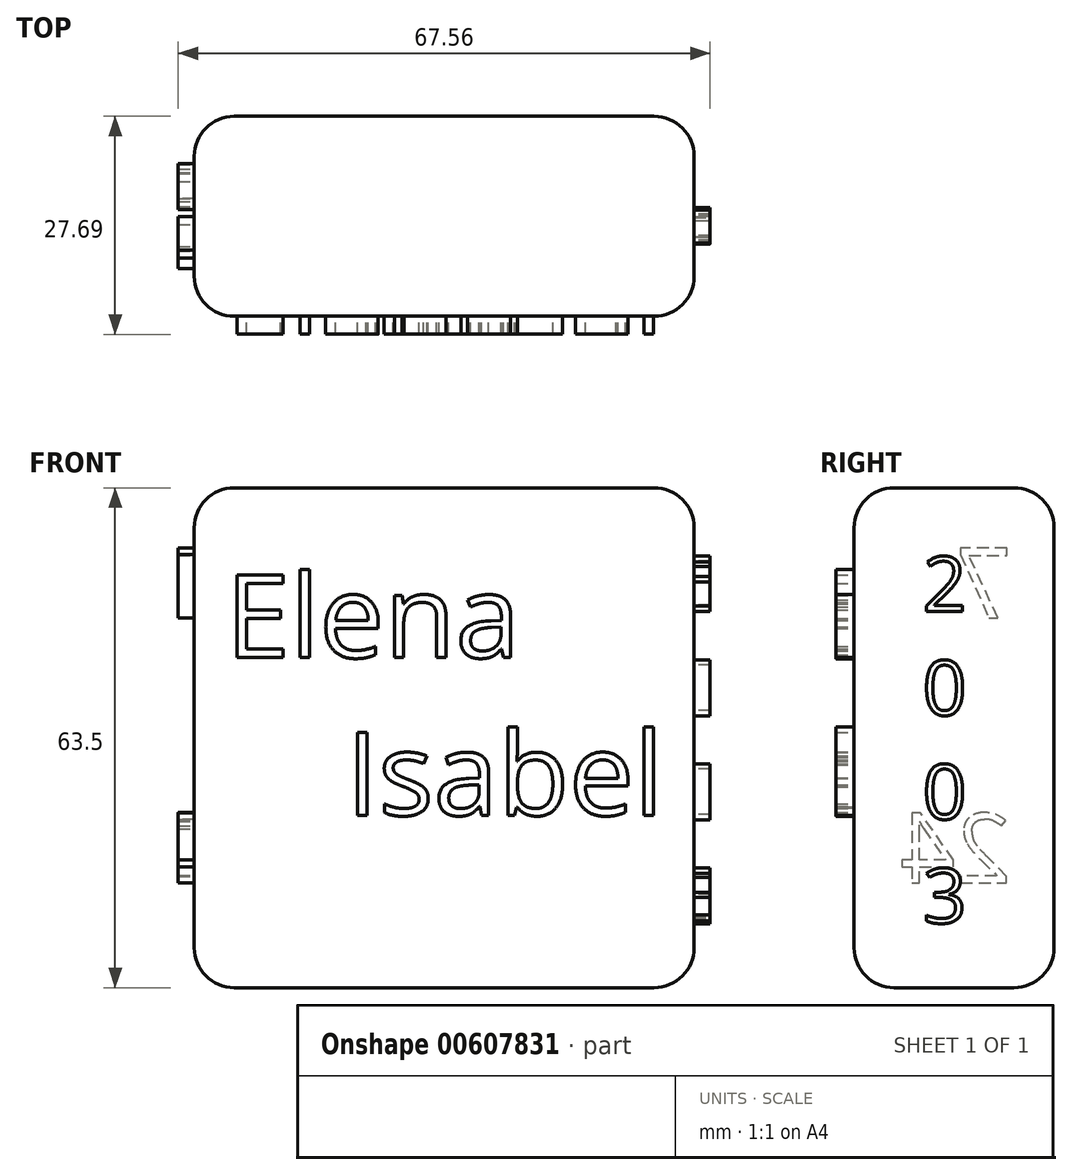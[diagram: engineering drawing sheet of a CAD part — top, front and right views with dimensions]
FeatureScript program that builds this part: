
annotation { "Feature Type Name" : "Feature", "Feature Type Description" : "" }
export const myFeature = defineFeature(function(context is Context, id is Id, definition is map)
    precondition{}
    {
        {
            var Q0;
            Q0=qCreatedBy(makeId("Front.planeOp"),FACE);
            var sketch = newSketch(context, id + "F0", { "sketchPlane" : qUnion([Q0])});
            skLineSegment(sketch, "E0.bottom", {"start": v(-39.04, 48.68) * mm, "end": v(24.46, 48.68) * mm});
            skLineSegment(sketch, "E0.top", {"start": v(-39.04, -14.82) * mm, "end": v(24.46, -14.82) * mm});
            skLineSegment(sketch, "E0.left", {"start": v(-39.04, 48.68) * mm, "end": v(-39.04, -14.82) * mm});
            skLineSegment(sketch, "E0.right", {"start": v(24.46, 48.68) * mm, "end": v(24.46, -14.82) * mm});
            skSolve(sketch);
        }
        {
            var Q0;
            Q0=makeQuery(id+"F0.imprint","IMPRINT",FACE,{"disambiguationData":[TD([[makeQuery(id+"F0.imprint","IMPRINT",EDGE,{"derivedFrom":sQuery(id+"F0.wireOp",EDGE,"E0.bottom")}),-1.0]])]});
            var sketch = newSketch(context, id + "F1", { "sketchPlane" : qUnion([Q0])});
            skText(sketch, "E1", { "text": "Elena \n    Isabel", "fontName": "OpenSans-Regular.ttf"});
            const initialGuessF1  = {"E1": [-0.03506, 0.02711, 1, 0, 0.0106]};
            skSetInitialGuess(sketch, initialGuessF1);
            skSolve(sketch);
        }
        {
            var Q0;
            Q0 = qSketchRegion(id + "F0", true);
            extrude(context, id + "F2", {"entities" : qUnion([Q0]), "depth" : 25.4 * mm, "offsetDistance" : 25.4 * mm});
        }
        {
            var Q0;
            Q0 = qSketchRegion(id + "F1", true);
            extrude(context, id + "F3", {"entities" : qUnion([Q0]), "operationType" : NewBodyOperationType.ADD, "depth" : 27.7 * mm, "offsetDistance" : 25.4 * mm});
        }
        {
            var Q0;
            Q0=makeQuery(id+"F2.opExtrude","SWEPT_FACE",FACE,{"disambiguationData":[OSD([sQuery(id+"F0.wireOp",EDGE,"E0.left")])]});
            var sketch = newSketch(context, id + "F4", { "sketchPlane" : qUnion([Q0])});
            skText(sketch, "E2", { "text": "7\n\n24", "fontName": "OpenSans-Regular.ttf"});
            const initialGuessF4  = {"E2": [0.00542, 0.03217, 1, 0, 0.00892]};
            skSetInitialGuess(sketch, initialGuessF4);
            skSolve(sketch);
        }
        {
            var Q0;
            Q0 = qSketchRegion(id + "F4", true);
            extrude(context, id + "F5", {"entities" : qUnion([Q0]), "operationType" : NewBodyOperationType.ADD, "depth" : 2.03 * mm, "offsetDistance" : 25.4 * mm});
        }
        {
            var Q0;
            Q0=makeQuery(id+"F2.opExtrude","SWEPT_FACE",FACE,{"disambiguationData":[OSD([sQuery(id+"F0.wireOp",EDGE,"E0.right")])]});
            var sketch = newSketch(context, id + "F6", { "sketchPlane" : qUnion([Q0])});
            skText(sketch, "E3", { "text": "2\n0\n0\n3", "fontName": "OpenSans-Regular.ttf"});
            const initialGuessF6  = {"E3": [-0.01667, 0.033, 1, 0, 0.00699]};
            skSetInitialGuess(sketch, initialGuessF6);
            skSolve(sketch);
        }
        {
            var Q0;
            Q0 = qSketchRegion(id + "F6", true);
            extrude(context, id + "F7", {"entities" : qUnion([Q0]), "operationType" : NewBodyOperationType.ADD, "depth" : 2.03 * mm, "offsetDistance" : 25.4 * mm});
        }
        {
            var Q0;
            Q0=makeQuery(id+"F2.opExtrude","CAP_EDGE",EDGE,{"disambiguationData":[OSD([sQuery(id+"F0.wireOp",EDGE,"E0.bottom")])],"isStart":false});
            var Q1;
            Q1=makeQuery(id+"F2.opExtrude","SWEPT_EDGE",EDGE,{"disambiguationData":[OSD([sQuery(id+"F0.wireOp",EDGE,"E0.bottom"),sQuery(id+"F0.wireOp",EDGE,"E0.right")])]});
            var Q2;
            Q2=makeQuery(id+"F2.opExtrude","CAP_EDGE",EDGE,{"disambiguationData":[OSD([sQuery(id+"F0.wireOp",EDGE,"E0.bottom")])],"isStart":true});
            var Q3;
            Q3=makeQuery(id+"F2.opExtrude","SWEPT_EDGE",EDGE,{"disambiguationData":[OSD([sQuery(id+"F0.wireOp",EDGE,"E0.bottom"),sQuery(id+"F0.wireOp",EDGE,"E0.left")])]});
            var Q4;
            Q4=makeQuery(id+"F2.opExtrude","CAP_EDGE",EDGE,{"disambiguationData":[OSD([sQuery(id+"F0.wireOp",EDGE,"E0.left")])],"isStart":true});
            var Q5;
            Q5=makeQuery(id+"F2.opExtrude","CAP_EDGE",EDGE,{"disambiguationData":[OSD([sQuery(id+"F0.wireOp",EDGE,"E0.top")])],"isStart":true});
            var Q6;
            Q6=makeQuery(id+"F2.opExtrude","SWEPT_EDGE",EDGE,{"disambiguationData":[OSD([sQuery(id+"F0.wireOp",EDGE,"E0.top"),sQuery(id+"F0.wireOp",EDGE,"E0.left")])]});
            var Q7;
            Q7=makeQuery(id+"F2.opExtrude","CAP_EDGE",EDGE,{"disambiguationData":[OSD([sQuery(id+"F0.wireOp",EDGE,"E0.right")])],"isStart":true});
            var Q8;
            Q8=makeQuery(id+"F2.opExtrude","CAP_EDGE",EDGE,{"disambiguationData":[OSD([sQuery(id+"F0.wireOp",EDGE,"E0.left")])],"isStart":false});
            var Q9;
            Q9=makeQuery(id+"F2.opExtrude","CAP_EDGE",EDGE,{"disambiguationData":[OSD([sQuery(id+"F0.wireOp",EDGE,"E0.top")])],"isStart":false});
            fillet(context, id + "F8", {"entities" : qUnion([Q0, Q1, Q2, Q3, Q4, Q5, Q6, Q7, Q8, Q9]), "radius" : 5.08 * mm, "tangentPropagation" : true, "allowEdgeOverflow" : false});
        }
        {
            var Q0;
            Q0=makeQuery(id+"F2.opExtrude","SWEPT_EDGE",EDGE,{"disambiguationData":[OSD([sQuery(id+"F0.wireOp",EDGE,"E0.top"),sQuery(id+"F0.wireOp",EDGE,"E0.right")])]});
            fillet(context, id + "F9", {"entities" : qUnion([Q0]), "radius" : 5.08 * mm, "tangentPropagation" : true, "allowEdgeOverflow" : false});
        }
    });
